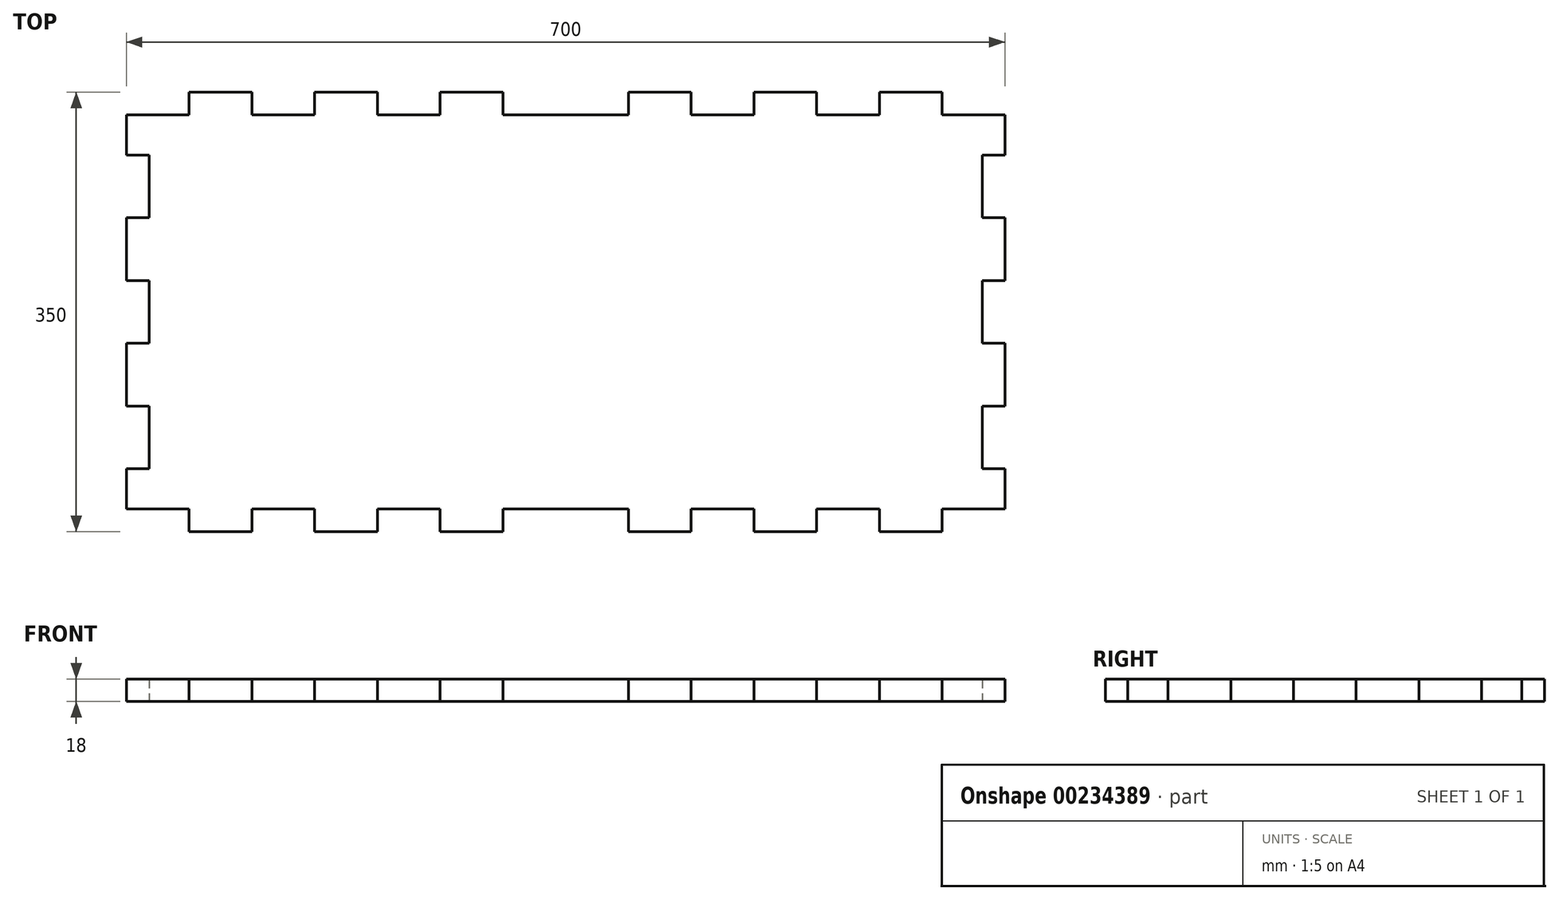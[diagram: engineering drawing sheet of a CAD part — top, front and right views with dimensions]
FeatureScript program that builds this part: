
annotation { "Feature Type Name" : "Feature", "Feature Type Description" : "" }
export const myFeature = defineFeature(function(context is Context, id is Id, definition is map)
    precondition{}
    {
        {
            var Q0;
            Q0=qCreatedBy(makeId("Top.planeOp"),FACE);
            var sketch = newSketch(context, id + "F0", { "sketchPlane" : qUnion([Q0])});
            skLineSegment(sketch, "E0.left", {"start": v(-350, -157) * mm, "end": v(-350, -125) * mm});
            skLineSegment(sketch, "E0.right", {"start": v(350, -157) * mm, "end": v(350, -125) * mm});
            skPoint(sketch, "E0.middle", {"position": v(0, 0) * mm});
            skLineSegment(sketch, "E1.right", {"start": v(-300, -175) * mm, "end": v(-300, -157) * mm});
            skLineSegment(sketch, "E2.right", {"start": v(-250, -157) * mm, "end": v(-250, -175) * mm});
            skLineSegment(sketch, "E3.right", {"start": v(-200, -157) * mm, "end": v(-200, -175) * mm});
            skLineSegment(sketch, "E4.right", {"start": v(-150, -157) * mm, "end": v(-150, -175) * mm});
            skLineSegment(sketch, "E5.right", {"start": v(-100, -157) * mm, "end": v(-100, -175) * mm});
            skLineSegment(sketch, "E6.right", {"start": v(-50, -157) * mm, "end": v(-50, -175) * mm});
            skLineSegment(sketch, "E7.bottom", {"start": v(0, -157) * mm, "end": v(50, -157) * mm});
            skLineSegment(sketch, "E7.right", {"start": v(50, -157) * mm, "end": v(50, -175) * mm});
            skLineSegment(sketch, "E8.top", {"start": v(50, -175) * mm, "end": v(100, -175) * mm});
            skLineSegment(sketch, "E8.right", {"start": v(100, -157) * mm, "end": v(100, -175) * mm});
            skLineSegment(sketch, "E9.bottom", {"start": v(100, -157) * mm, "end": v(150, -157) * mm});
            skLineSegment(sketch, "E9.right", {"start": v(150, -157) * mm, "end": v(150, -175) * mm});
            skLineSegment(sketch, "E10.top", {"start": v(150, -175) * mm, "end": v(200, -175) * mm});
            skLineSegment(sketch, "E10.right", {"start": v(200, -157) * mm, "end": v(200, -175) * mm});
            skLineSegment(sketch, "E11.bottom", {"start": v(200, -157) * mm, "end": v(250, -157) * mm});
            skLineSegment(sketch, "E11.right", {"start": v(250, -157) * mm, "end": v(250, -175) * mm});
            skLineSegment(sketch, "E12.top", {"start": v(250, -175) * mm, "end": v(300, -175) * mm});
            skLineSegment(sketch, "E12.right", {"start": v(300, -157) * mm, "end": v(300, -175) * mm});
            skLineSegment(sketch, "E13.bottom", {"start": v(300, -157) * mm, "end": v(350, -157) * mm});
            skPoint(sketch, "E14.orphan", {"position": v(350, -175) * mm});
            skLineSegment(sketch, "E15.top", {"start": v(-350, -125) * mm, "end": v(-332, -125) * mm});
            skLineSegment(sketch, "E16.bottom", {"start": v(-332, -125) * mm, "end": v(-350, -125) * mm});
            skLineSegment(sketch, "E16.top", {"start": v(-332, -75) * mm, "end": v(-350, -75) * mm});
            skLineSegment(sketch, "E16.left", {"start": v(-332, -125) * mm, "end": v(-332, -75) * mm});
            skLineSegment(sketch, "E17.top", {"start": v(-332, -25) * mm, "end": v(-350, -25) * mm});
            skLineSegment(sketch, "E17.right", {"start": v(-350, -75) * mm, "end": v(-350, -25) * mm});
            skLineSegment(sketch, "E18.top", {"start": v(-332, 25) * mm, "end": v(-350, 25) * mm});
            skLineSegment(sketch, "E18.left", {"start": v(-332, -25) * mm, "end": v(-332, 25) * mm});
            skLineSegment(sketch, "E19.top", {"start": v(-332, 75) * mm, "end": v(-350, 75) * mm});
            skLineSegment(sketch, "E19.right", {"start": v(-350, 25) * mm, "end": v(-350, 75) * mm});
            skLineSegment(sketch, "E20.top", {"start": v(-332, 125) * mm, "end": v(-350, 125) * mm});
            skLineSegment(sketch, "E20.left", {"start": v(-332, 75) * mm, "end": v(-332, 125) * mm});
            skLineSegment(sketch, "E21.right", {"start": v(-350, 125) * mm, "end": v(-350, 157) * mm});
            skLineSegment(sketch, "E22.bottom", {"start": v(350, -157) * mm, "end": v(332, -157) * mm});
            skLineSegment(sketch, "E22.top", {"start": v(350, -125) * mm, "end": v(332, -125) * mm});
            skLineSegment(sketch, "E23.bottom", {"start": v(332, -125) * mm, "end": v(350, -125) * mm});
            skLineSegment(sketch, "E23.top", {"start": v(332, -75) * mm, "end": v(350, -75) * mm});
            skLineSegment(sketch, "E23.left", {"start": v(332, -125) * mm, "end": v(332, -75) * mm});
            skLineSegment(sketch, "E24.top", {"start": v(332, -25) * mm, "end": v(350, -25) * mm});
            skLineSegment(sketch, "E24.right", {"start": v(350, -75) * mm, "end": v(350, -25) * mm});
            skLineSegment(sketch, "E25.top", {"start": v(332, 25) * mm, "end": v(350, 25) * mm});
            skLineSegment(sketch, "E25.left", {"start": v(332, -25) * mm, "end": v(332, 25) * mm});
            skLineSegment(sketch, "E26.top", {"start": v(332, 75) * mm, "end": v(350, 75) * mm});
            skLineSegment(sketch, "E26.right", {"start": v(350, 25) * mm, "end": v(350, 75) * mm});
            skLineSegment(sketch, "E27.top", {"start": v(332, 125) * mm, "end": v(350, 125) * mm});
            skLineSegment(sketch, "E27.left", {"start": v(332, 75) * mm, "end": v(332, 125) * mm});
            skLineSegment(sketch, "E28.right", {"start": v(350, 125) * mm, "end": v(350, 157) * mm});
            skLineSegment(sketch, "E29.right", {"start": v(300, 175) * mm, "end": v(300, 157) * mm});
            skLineSegment(sketch, "E30.left", {"start": v(300, 157) * mm, "end": v(300, 175) * mm});
            skLineSegment(sketch, "E30.right", {"start": v(250, 157) * mm, "end": v(250, 175) * mm});
            skLineSegment(sketch, "E31.right", {"start": v(200, 157) * mm, "end": v(200, 175) * mm});
            skLineSegment(sketch, "E32.right", {"start": v(150, 157) * mm, "end": v(150, 175) * mm});
            skLineSegment(sketch, "E33.right", {"start": v(100, 157) * mm, "end": v(100, 175) * mm});
            skLineSegment(sketch, "E34.right", {"start": v(50, 157) * mm, "end": v(50, 175) * mm});
            skLineSegment(sketch, "E35.bottom", {"start": v(0, 157) * mm, "end": v(-50, 157) * mm});
            skLineSegment(sketch, "E35.right", {"start": v(-50, 157) * mm, "end": v(-50, 175) * mm});
            skLineSegment(sketch, "E36.top", {"start": v(-50, 175) * mm, "end": v(-100, 175) * mm});
            skLineSegment(sketch, "E36.right", {"start": v(-100, 157) * mm, "end": v(-100, 175) * mm});
            skLineSegment(sketch, "E37.bottom", {"start": v(-100, 157) * mm, "end": v(-150, 157) * mm});
            skLineSegment(sketch, "E37.right", {"start": v(-150, 157) * mm, "end": v(-150, 175) * mm});
            skLineSegment(sketch, "E38.top", {"start": v(-150, 175) * mm, "end": v(-200, 175) * mm});
            skLineSegment(sketch, "E38.right", {"start": v(-200, 157) * mm, "end": v(-200, 175) * mm});
            skLineSegment(sketch, "E39.bottom", {"start": v(-200, 157) * mm, "end": v(-250, 157) * mm});
            skLineSegment(sketch, "E39.right", {"start": v(-250, 157) * mm, "end": v(-250, 175) * mm});
            skLineSegment(sketch, "E40.top", {"start": v(-250, 175) * mm, "end": v(-300, 175) * mm});
            skLineSegment(sketch, "E40.right", {"start": v(-300, 157) * mm, "end": v(-300, 175) * mm});
            skLineSegment(sketch, "E41.bottom", {"start": v(-300, 157) * mm, "end": v(-350, 157) * mm});
            skLineSegment(sketch, "E42.trimOffspring", {"start": v(-300, 175) * mm, "end": v(-250, 175) * mm});
            skPoint(sketch, "E43.orphan", {"position": v(-350, 175) * mm});
            skLineSegment(sketch, "E44.trimOffspring", {"start": v(-100, 175) * mm, "end": v(-50, 175) * mm});
            skLineSegment(sketch, "E45.trimOffspring", {"start": v(-200, 175) * mm, "end": v(-150, 175) * mm});
            skLineSegment(sketch, "E46", {"start": v(-300, -175) * mm, "end": v(-250, -175) * mm});
            skLineSegment(sketch, "E47", {"start": v(-200, -175) * mm, "end": v(-150, -175) * mm});
            skLineSegment(sketch, "E48", {"start": v(-100, -175) * mm, "end": v(-50, -175) * mm});
            skLineSegment(sketch, "E49", {"start": v(-50, -157) * mm, "end": v(0, -157) * mm});
            skLineSegment(sketch, "E50", {"start": v(-150, -157) * mm, "end": v(-100, -157) * mm});
            skLineSegment(sketch, "E51", {"start": v(-250, -157) * mm, "end": v(-200, -157) * mm});
            skLineSegment(sketch, "E52", {"start": v(-350, -157) * mm, "end": v(-300, -157) * mm});
            skPoint(sketch, "E53.orphan", {"position": v(-350, -175) * mm});
            skLineSegment(sketch, "E54", {"start": v(0, 157) * mm, "end": v(50, 157) * mm});
            skLineSegment(sketch, "E55", {"start": v(100, 175) * mm, "end": v(50, 175) * mm});
            skLineSegment(sketch, "E56", {"start": v(100, 157) * mm, "end": v(150, 157) * mm});
            skLineSegment(sketch, "E57", {"start": v(150, 175) * mm, "end": v(200, 175) * mm});
            skLineSegment(sketch, "E58", {"start": v(250, 175) * mm, "end": v(300, 175) * mm});
            skLineSegment(sketch, "E59", {"start": v(200, 157) * mm, "end": v(250, 157) * mm});
            skLineSegment(sketch, "E60", {"start": v(300, 157) * mm, "end": v(350, 157) * mm});
            skPoint(sketch, "E61.orphan", {"position": v(350, 175) * mm});
            skSolve(sketch);
        }
        {
            var Q0;
            Q0 = qSketchRegion(id + "F0", true);
            extrude(context, id + "F1", {"entities" : qUnion([Q0]), "depth" : 18 * mm});
        }
    });
